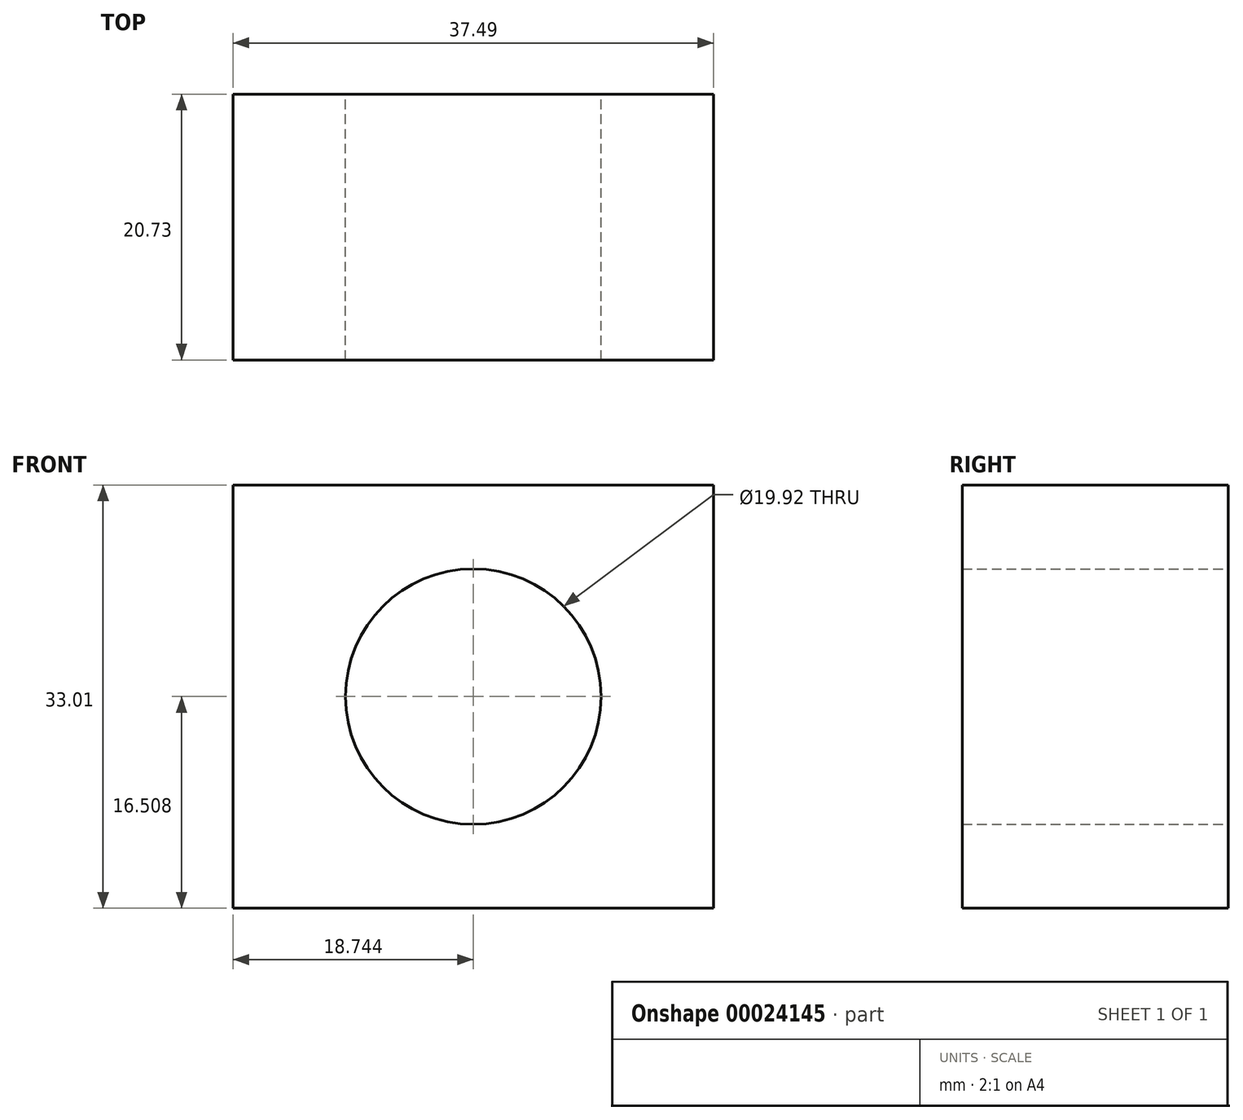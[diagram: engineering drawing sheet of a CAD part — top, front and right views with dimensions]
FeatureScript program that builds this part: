
annotation { "Feature Type Name" : "Feature", "Feature Type Description" : "" }
export const myFeature = defineFeature(function(context is Context, id is Id, definition is map)
    precondition{}
    {
        {
            var Q0;
            Q0=qCreatedBy(makeId("Front.planeOp"),FACE);
            var sketch = newSketch(context, id + "F0", { "sketchPlane" : qUnion([Q0])});
            skLineSegment(sketch, "E0.rect.bottom", {"start": v(-20.42, 31.61) * mm, "end": v(-57.9, 31.61) * mm});
            skLineSegment(sketch, "E0.rect.top", {"start": v(-20.42, 64.62) * mm, "end": v(-57.9, 64.62) * mm});
            skLineSegment(sketch, "E0.rect.left", {"start": v(-20.42, 31.61) * mm, "end": v(-20.42, 64.62) * mm});
            skLineSegment(sketch, "E0.rect.right", {"start": v(-57.9, 31.61) * mm, "end": v(-57.9, 64.62) * mm});
            skPoint(sketch, "E0.rect.middle", {"position": v(-39.17, 48.12) * mm});
            skCircle(sketch, "E1", {"center": v(-39.17, 48.12) * mm, "radius": 9.96 * mm});
            skSolve(sketch);
        }
        {
            var Q0;
            Q0 = qSketchRegion(id + "F0", true);
            extrude(context, id + "F1", {"entities" : qUnion([Q0]), "depth" : 20.73 * mm});
        }
    });
